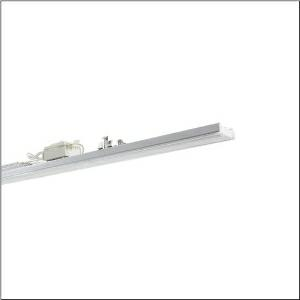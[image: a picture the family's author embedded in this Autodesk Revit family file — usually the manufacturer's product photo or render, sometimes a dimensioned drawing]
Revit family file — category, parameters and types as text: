
# Revit family: licross_r__21_recessed_ho_52te1ecn4cxs_0519
name_source: partatom
category: Lighting Fixtures
units: mm (PartAtom-declared; Revit-internal decimal feet)

## family parameters
Cut with Voids When Loaded = No
Host = Face
Light Source = No
Part Type = Normal
Room Calculation Point = No
Round Connector Dimension = Use Diameter
Shared = No

## types (1)
- --- (1 x LED, 12350 lm, 68.4 W, 4000K)
    Apparent Load = 68 VA
    CIE Flux Codes = 85 95 99 100 100
    Color Rendering = 80
    Color Temperature = 4000K
    Default Elevation = 1800 mm
    Description = Licross® 21 Recessed HO, luminaire insert, of sheet steel, galvanised, coil coated, white, length: 1.500mm, width: 66mm, height: 67mm, LED rated luminous flux: 12.350lm, light colour: 840, control gear: ON/OFF Multilumen, CLOi, control gear: ECG Multilumen, with plug, 3-pole, with phase selection, mains connection: 220..240V, AC, 50/60Hz, start of lifetime: 69W, end of service life: 83W, halogen-free wiring, primary light control with lens, of plastic, primary optical cover: cover, of PMMA, light emission: direct distribution, primary light characteristic: symmetric, protection rating (complete): IP54, insulation class (complete): insulation class I (protective earthing), certification: CE, ENEC, VDE, UKCA, protection symbol: D if used in an environment with non-conductive dust loads with corresponding accessories, impact resistance: IK06, permissible ambient temperature for indoor applications: -35..+30°C, corresponds to IFS (International Featured Standards) requirements for safety and quality in the food industry, reducing of maximum allowable ambient temperature of 5°C with ceiling mounting, LABS conformity tested according to VDMA 24364:2018-05, packaging unit: 1 piece
    Height = 58 mm
    Lamp = 1 x LED
    Lamp Light Flux = 12350 lm
    Lamp Power = 68.4 W
    Lamp count = 1
    Length = 1500 mm
    Luminous efficacy = 181 lm/W
    Manufacturer = Siteco
    ModVariant = No
    Model = 52TE1ECN4CXS
    Mounting Place = Ceiling
    Mounting Type = Pendant
    Number of Poles = 1
    OnlyDefault = Yes
    Power Factor = 1
    Product Name = Licross® 21 Recessed HO
    Product group = luminaire insert
    ProductGroupID = 902
    Protection Class = Protection class I
    Protection Degree = IP 54
    RLX_Detail_Level = 1
    RLX_Emergency_Light_Flux = 0 lm
    RLX_Emergency_Type = 0
    RLX_Emergency_Type_DB = No
    RlxData = <blob elided: 22445 chars, md5=fc968ca6>
    Socket = socket
    Standby Power = 0 W
    System Light Flux = 12350 lm
    System Power = 68 W
    Type Comments = factory setting: luminous flux: 100 % | (A | C | E) | 161 mA
    Type Image = l_1296930.jpg
    URL = http://relux.com
    VarID = @adj_109906
    Voltage = 0 V
    Weight = 0.00 kg
    Width = 66 mm

## geometry (parser evidence)
native form markers: Blend x4, Sweep x10
no freeform markers — native parametric forms only
